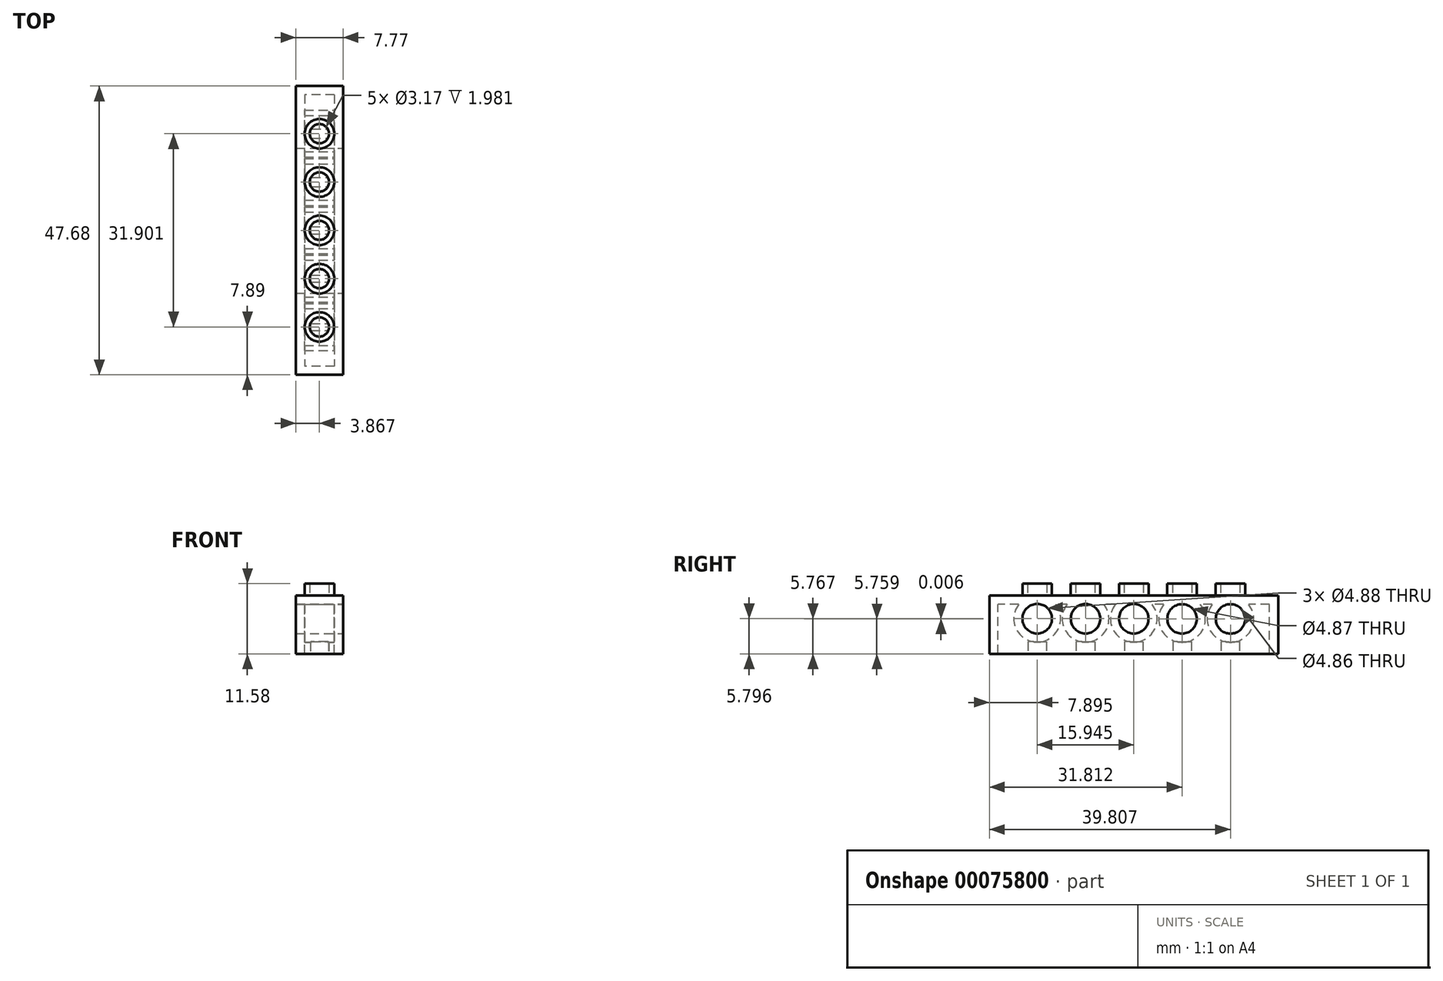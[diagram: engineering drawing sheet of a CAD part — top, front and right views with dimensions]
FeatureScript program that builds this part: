
annotation { "Feature Type Name" : "Feature", "Feature Type Description" : "" }
export const myFeature = defineFeature(function(context is Context, id is Id, definition is map)
    precondition{}
    {
        {
            var Q0;
            Q0=qCreatedBy(makeId("Right.planeOp"),FACE);
            var sketch = newSketch(context, id + "F0", { "sketchPlane" : qUnion([Q0])});
            skLineSegment(sketch, "E0.bottom", {"start": v(23.84, -4.8) * mm, "end": v(-23.84, -4.8) * mm});
            skLineSegment(sketch, "E0.top", {"start": v(23.84, 4.8) * mm, "end": v(-23.84, 4.8) * mm});
            skLineSegment(sketch, "E0.left", {"start": v(23.84, -4.8) * mm, "end": v(23.84, 4.8) * mm});
            skLineSegment(sketch, "E0.right", {"start": v(-23.84, -4.8) * mm, "end": v(-23.84, 4.8) * mm});
            skPoint(sketch, "E0.middle", {"position": v(0, 0) * mm});
            skSolve(sketch);
        }
        {
            var Q0;
            Q0=makeQuery(id+"F0.imprint","IMPRINT",FACE,{"disambiguationData":[TD([[makeQuery(id+"F0.imprint","IMPRINT",EDGE,{"derivedFrom":sQuery(id+"F0.wireOp",EDGE,"E0.bottom")}),-1.0]])]});
            extrude(context, id + "F1", {"entities" : qUnion([Q0]), "depth" : 7.77 * mm});
        }
        {
            var Q0;
            Q0=makeQuery(id+"F1.opExtrude","CAP_FACE",FACE,{"disambiguationData":[OSD([sQuery(id+"F0.wireOp",EDGE,"E0.bottom"),sQuery(id+"F0.wireOp",EDGE,"E0.top"),sQuery(id+"F0.wireOp",EDGE,"E0.left"),sQuery(id+"F0.wireOp",EDGE,"E0.right")])],"isStart":false});
            var sketch = newSketch(context, id + "F2", { "sketchPlane" : qUnion([Q0])});
            skCircle(sketch, "E1", {"center": v(0, 1) * mm, "radius": 2.44 * mm});
            skSolve(sketch);
        }
        {
            var Q0;
            Q0=makeQuery(id+"F2.imprint","IMPRINT",FACE,{"disambiguationData":[TD([[makeQuery(id+"F2.imprint","IMPRINT",EDGE,{"derivedFrom":sQuery(id+"F2.wireOp",EDGE,"E1")}),-1.0]])]});
            var sketch = newSketch(context, id + "F3", { "sketchPlane" : qUnion([Q0])});
            skCircle(sketch, "E2", {"center": v(7.97, 0.97) * mm, "radius": 2.44 * mm});
            skSolve(sketch);
        }
        {
            var Q0;
            Q0=makeQuery(id+"F2.imprint","IMPRINT",FACE,{"disambiguationData":[TD([[makeQuery(id+"F2.imprint","IMPRINT",EDGE,{"derivedFrom":sQuery(id+"F2.wireOp",EDGE,"E1")}),-1.0]])]});
            var sketch = newSketch(context, id + "F4", { "sketchPlane" : qUnion([Q0])});
            skCircle(sketch, "E3", {"center": v(15.97, 0.96) * mm, "radius": 2.43 * mm});
            skSolve(sketch);
        }
        {
            var Q0;
            Q0=makeQuery(id+"F2.imprint","IMPRINT",FACE,{"disambiguationData":[TD([[makeQuery(id+"F2.imprint","IMPRINT",EDGE,{"derivedFrom":sQuery(id+"F2.wireOp",EDGE,"E1")}),-1.0]])]});
            var sketch = newSketch(context, id + "F5", { "sketchPlane" : qUnion([Q0])});
            skCircle(sketch, "E4", {"center": v(-7.97, 1) * mm, "radius": 2.44 * mm});
            skSolve(sketch);
        }
        {
            var Q0;
            Q0=makeQuery(id+"F2.imprint","IMPRINT",FACE,{"disambiguationData":[TD([[makeQuery(id+"F2.imprint","IMPRINT",EDGE,{"derivedFrom":sQuery(id+"F2.wireOp",EDGE,"E1")}),-1.0]])]});
            var sketch = newSketch(context, id + "F6", { "sketchPlane" : qUnion([Q0])});
            skCircle(sketch, "E5", {"center": v(-15.95, 1) * mm, "radius": 2.44 * mm});
            skSolve(sketch);
        }
        {
            var Q0;
            Q0=makeQuery(id+"F2.imprint","IMPRINT",FACE,{"disambiguationData":[TD([[makeQuery(id+"F2.imprint","IMPRINT",EDGE,{"derivedFrom":sQuery(id+"F2.wireOp",EDGE,"E1")}),1.0]])]});
            var Q1;
            Q1=makeQuery(id+"F1.opExtrude","CAP_FACE",FACE,{"disambiguationData":[OSD([sQuery(id+"F0.wireOp",EDGE,"E0.bottom"),sQuery(id+"F0.wireOp",EDGE,"E0.top"),sQuery(id+"F0.wireOp",EDGE,"E0.left"),sQuery(id+"F0.wireOp",EDGE,"E0.right")])],"isStart":true});
            extrude(context, id + "F7", {"entities" : qUnion([Q0]), "operationType" : NewBodyOperationType.REMOVE, "endBound" : BoundingType.UP_TO_SURFACE, "oppositeDirection" : true, "endBoundEntityFace" : qUnion([Q1]), "depth" : 25.4 * mm});
        }
        {
            var Q0;
            Q0 = qSketchRegion(id + "F3", true);
            var Q1;
            Q1 = qSketchRegion(id + "F4", true);
            var Q2;
            Q2 = qSketchRegion(id + "F5", true);
            var Q3;
            Q3 = qSketchRegion(id + "F6", true);
            var Q4;
            Q4=sQuery(id+"F6.wireOp",EDGE,"E5");
            var Q5;
            Q5=makeQuery(id+"F1.opExtrude","CAP_FACE",FACE,{"disambiguationData":[OSD([sQuery(id+"F0.wireOp",EDGE,"E0.bottom"),sQuery(id+"F0.wireOp",EDGE,"E0.top"),sQuery(id+"F0.wireOp",EDGE,"E0.left"),sQuery(id+"F0.wireOp",EDGE,"E0.right")])],"isStart":true});
            extrude(context, id + "F8", {"entities" : qUnion([Q0, Q1, Q2, Q3]), "operationType" : NewBodyOperationType.REMOVE, "surfaceEntities" : qUnion([Q4]), "endBound" : BoundingType.UP_TO_SURFACE, "oppositeDirection" : true, "endBoundEntityFace" : qUnion([Q5]), "depth" : 25.4 * mm});
        }
        {
            var Q0;
            Q0=makeQuery(id+"F1.opExtrude","SWEPT_FACE",FACE,{"disambiguationData":[OSD([sQuery(id+"F0.wireOp",EDGE,"E0.top")])]});
            var sketch = newSketch(context, id + "F9", { "sketchPlane" : qUnion([Q0])});
            skLineSegment(sketch, "E6", {"start": v(3.87, 0) * mm, "end": v(7.86, 0) * mm});
            skCircle(sketch, "E7", {"center": v(3.87, -7.98) * mm, "radius": 2.44 * mm});
            skCircle(sketch, "E8", {"center": v(3.87, -15.95) * mm, "radius": 2.43 * mm});
            skCircle(sketch, "E9", {"center": v(3.87, 7.98) * mm, "radius": 2.44 * mm});
            skCircle(sketch, "E10", {"center": v(3.87, 15.95) * mm, "radius": 2.44 * mm});
            skSolve(sketch);
        }
        {
            var Q0;
            Q0=makeQuery(id+"F9.imprint","IMPRINT",FACE,{"disambiguationData":[TD([[makeQuery(id+"F9.imprint","IMPRINT",EDGE,{"derivedFrom":sQuery(id+"F9.wireOp",EDGE,"E10")}),1.0]])]});
            var Q1;
            Q1=makeQuery(id+"F9.imprint","IMPRINT",FACE,{"disambiguationData":[TD([[makeQuery(id+"F9.imprint","IMPRINT",EDGE,{"derivedFrom":sQuery(id+"F9.wireOp",EDGE,"E9")}),1.0]])]});
            var Q2;
            Q2=makeQuery(id+"F9.imprint","IMPRINT",FACE,{"disambiguationData":[TD([[makeQuery(id+"F9.imprint","IMPRINT",EDGE,{"derivedFrom":sQuery(id+"F9.wireOp",EDGE,"E7")}),1.0]])]});
            var Q3;
            Q3=makeQuery(id+"F9.imprint","IMPRINT",FACE,{"disambiguationData":[TD([[makeQuery(id+"F9.imprint","IMPRINT",EDGE,{"derivedFrom":sQuery(id+"F9.wireOp",EDGE,"E8")}),1.0]])]});
            var Q4;
            Q4=sQuery(id+"F9.wireOp",EDGE,"E10");
            var Q5;
            Q5=sQuery(id+"F9.wireOp",EDGE,"E9");
            var Q6;
            Q6=sQuery(id+"F9.wireOp",EDGE,"E7");
            var Q7;
            Q7=sQuery(id+"F9.wireOp",EDGE,"E8");
            extrude(context, id + "F10", {"entities" : qUnion([Q0, Q1, Q2, Q3]), "operationType" : NewBodyOperationType.ADD, "surfaceEntities" : qUnion([Q4, Q5, Q6, Q7]), "depth" : 1.98 * mm});
        }
        {
            var Q0;
            Q0=makeQuery(id+"F1.opExtrude","SWEPT_FACE",FACE,{"disambiguationData":[OSD([sQuery(id+"F0.wireOp",EDGE,"E0.top")])]});
            var sketch = newSketch(context, id + "F11", { "sketchPlane" : qUnion([Q0])});
            skCircle(sketch, "E11", {"center": v(3.87, 0) * mm, "radius": 2.44 * mm});
            skSolve(sketch);
        }
        {
            var Q0;
            Q0 = qSketchRegion(id + "F11", true);
            var Q1;
            Q1=sQuery(id+"F11.wireOp",EDGE,"E11");
            extrude(context, id + "F12", {"entities" : qUnion([Q0]), "surfaceEntities" : qUnion([Q1]), "depth" : 1.98 * mm});
        }
        {
            var Q0;
            Q0=makeQuery(id+"F1.opExtrude","SWEPT_FACE",FACE,{"disambiguationData":[OSD([sQuery(id+"F0.wireOp",EDGE,"E0.top")])]});
            var sketch = newSketch(context, id + "F13", { "sketchPlane" : qUnion([Q0])});
            skCircle(sketch, "E12", {"center": v(3.87, -15.95) * mm, "radius": 1.59 * mm});
            skCircle(sketch, "E13", {"center": v(3.87, -7.98) * mm, "radius": 1.59 * mm});
            skCircle(sketch, "E14", {"center": v(3.87, 0) * mm, "radius": 1.59 * mm});
            skCircle(sketch, "E15", {"center": v(3.87, 7.98) * mm, "radius": 1.59 * mm});
            skCircle(sketch, "E16", {"center": v(3.87, 15.95) * mm, "radius": 1.59 * mm});
            skSolve(sketch);
        }
        {
            var Q0;
            Q0 = qSketchRegion(id + "F13", true);
            var Q1;
            Q1=makeQuery(id+"F10.opExtrude","CAP_FACE",FACE,{"disambiguationData":[OSD([sQuery(id+"F9.wireOp",EDGE,"E9")])],"isStart":false});
            extrude(context, id + "F14", {"entities" : qUnion([Q0]), "operationType" : NewBodyOperationType.REMOVE, "endBound" : BoundingType.UP_TO_SURFACE, "endBoundEntityFace" : qUnion([Q1]), "depth" : 1.98 * mm});
        }
        {
            var Q0;
            Q0=makeQuery(id+"F1.opExtrude","SWEPT_FACE",FACE,{"disambiguationData":[OSD([sQuery(id+"F0.wireOp",EDGE,"E0.bottom")])]});
            shell(context, id + "F15", {"entities" : qUnion([Q0]), "thickness" : 1.42 * mm});
        }
        {
            var Q0;
            Q0=makeQuery(id+"F1.opExtrude","SWEPT_FACE",FACE,{"disambiguationData":[OSD([sQuery(id+"F0.wireOp",EDGE,"E0.bottom")])]});
            var sketch = newSketch(context, id + "F16", { "sketchPlane" : qUnion([Q0])});
            skPoint(sketch, "E17.endSnap0", {"position": v(1.42, 0) * mm});
            skCircle(sketch, "E18", {"center": v(3.88, 0) * mm, "radius": 1.52 * mm});
            skCircle(sketch, "E19", {"center": v(3.88, 7.98) * mm, "radius": 1.53 * mm});
            skCircle(sketch, "E20", {"center": v(3.88, 15.95) * mm, "radius": 1.53 * mm});
            skCircle(sketch, "E21", {"center": v(3.88, -7.97) * mm, "radius": 1.52 * mm});
            skCircle(sketch, "E22", {"center": v(3.88, -15.95) * mm, "radius": 1.52 * mm});
            skSolve(sketch);
        }
        {
            var Q0;
            Q0=makeQuery(id+"F16.imprint","IMPRINT",FACE,{"disambiguationData":[TD([[makeQuery(id+"F16.imprint","IMPRINT",EDGE,{"derivedFrom":sQuery(id+"F16.wireOp",EDGE,"E22")}),1.0]])]});
            var Q1;
            Q1=makeQuery(id+"F16.imprint","IMPRINT",FACE,{"disambiguationData":[TD([[makeQuery(id+"F16.imprint","IMPRINT",EDGE,{"derivedFrom":sQuery(id+"F16.wireOp",EDGE,"E21")}),1.0]])]});
            var Q2;
            Q2=makeQuery(id+"F16.imprint","IMPRINT",FACE,{"disambiguationData":[TD([[makeQuery(id+"F16.imprint","IMPRINT",EDGE,{"derivedFrom":sQuery(id+"F16.wireOp",EDGE,"E18")}),1.0]])]});
            var Q3;
            Q3=makeQuery(id+"F16.imprint","IMPRINT",FACE,{"disambiguationData":[TD([[makeQuery(id+"F16.imprint","IMPRINT",EDGE,{"derivedFrom":sQuery(id+"F16.wireOp",EDGE,"E19")}),1.0]])]});
            var Q4;
            Q4=makeQuery(id+"F16.imprint","IMPRINT",FACE,{"disambiguationData":[TD([[makeQuery(id+"F16.imprint","IMPRINT",EDGE,{"derivedFrom":sQuery(id+"F16.wireOp",EDGE,"E20")}),1.0]])]});
            var Q5;
            Q5=sQuery(id+"F16.wireOp",EDGE,"E22");
            var Q6;
            Q6=sQuery(id+"F16.wireOp",EDGE,"E21");
            var Q7;
            Q7=sQuery(id+"F16.wireOp",EDGE,"E18");
            var Q8;
            Q8=sQuery(id+"F16.wireOp",EDGE,"E19");
            var Q9;
            Q9=sQuery(id+"F16.wireOp",EDGE,"E20");
            extrude(context, id + "F17", {"entities" : qUnion([Q0, Q1, Q2, Q3, Q4]), "operationType" : NewBodyOperationType.ADD, "surfaceEntities" : qUnion([Q5, Q6, Q7, Q8, Q9]), "oppositeDirection" : true, "depth" : 1.98 * mm});
        }
    });
